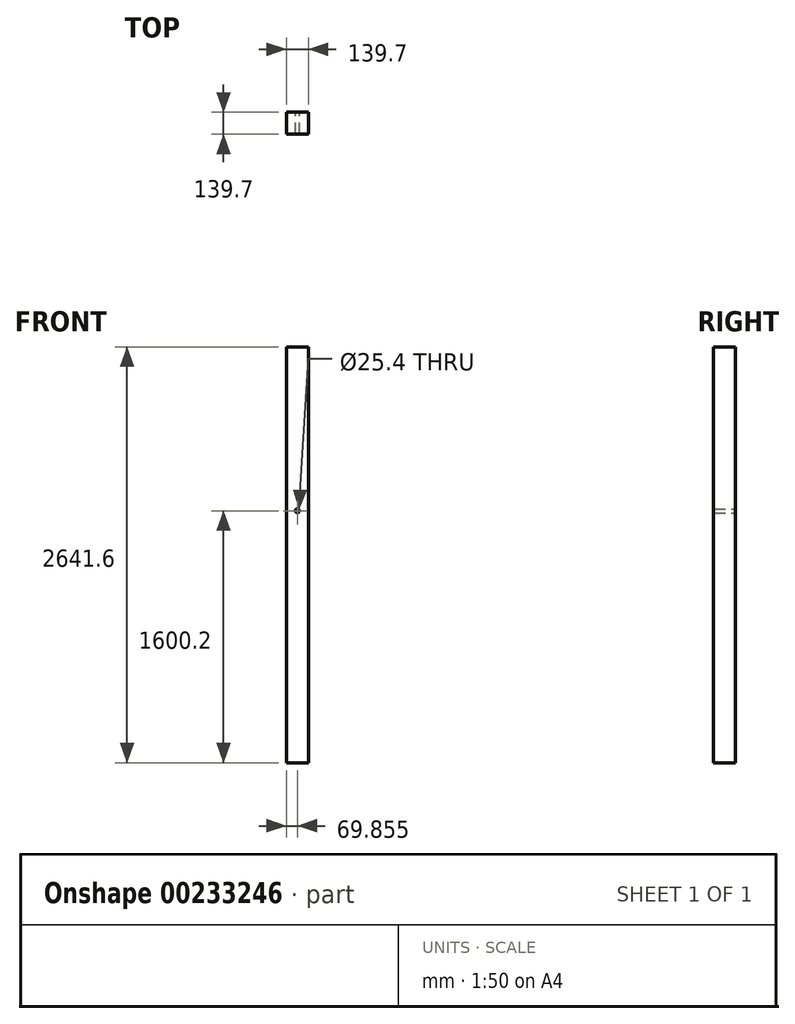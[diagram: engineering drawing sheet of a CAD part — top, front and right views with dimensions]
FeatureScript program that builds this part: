
annotation { "Feature Type Name" : "Feature", "Feature Type Description" : "" }
export const myFeature = defineFeature(function(context is Context, id is Id, definition is map)
    precondition{}
    {
        {
            var Q0;
            Q0=qCreatedBy(makeId("Front.planeOp"),FACE);
            var sketch = newSketch(context, id + "F0", { "sketchPlane" : qUnion([Q0])});
            skLineSegment(sketch, "E0.bottom", {"start": v(-70.5, 2508.3) * mm, "end": v(69.2, 2508.3) * mm});
            skLineSegment(sketch, "E0.top", {"start": v(-70.5, -133.3) * mm, "end": v(69.2, -133.3) * mm});
            skLineSegment(sketch, "E0.left", {"start": v(-70.5, 2508.3) * mm, "end": v(-70.5, -133.3) * mm});
            skLineSegment(sketch, "E0.right", {"start": v(69.2, 2508.3) * mm, "end": v(69.2, -133.3) * mm});
            skCircle(sketch, "E1", {"center": v(-0.65, 1466.9) * mm, "radius": 12.7 * mm});
            skSolve(sketch);
        }
        {
            var Q0;
            Q0 = qSketchRegion(id + "F0", true);
            extrude(context, id + "F1", {"entities" : qUnion([Q0]), "depth" : 139.7 * mm});
        }
    });
